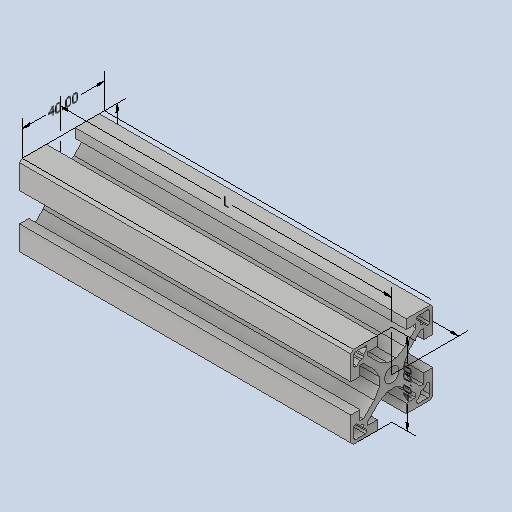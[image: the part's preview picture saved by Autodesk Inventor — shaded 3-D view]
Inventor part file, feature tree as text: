
AUTODESK INVENTOR PART (.ipt)
format: ipt  version: 2023 (Build 270158000, 158)  size: 289,792 bytes
history: native  units: mm
features: other x125, extrude x1, sketch x1
ambient origin geometry x8: Origin, YZ Plane, XZ Plane, XY Plane, X Axis, Y Axis, Z Axis, Center Point
bodies: Solid1 (feature_tree)
feature tree (127):
  other  "Annotations"
  extrude  "Extrusion1"  [1 undecoded]
  other  "CS_ANBAU_HINTEN_LINKS_XY"
  other  "CS_ANBAU_HINTEN_LINKS_YZ"
  other  "CS_ANBAU_HINTEN_LINKS_ZX"
  other  "CS_ANBAU_HINTEN_LINKS_X"
  other  "CS_ANBAU_HINTEN_LINKS_Y"
  other  "CS_ANBAU_HINTEN_LINKS_Z"
  other  "CS_ANBAU_HINTEN_LINKS_Center"
  other  "CS_ANBAU_HINTEN_OBEN_XY"
  other  "CS_ANBAU_HINTEN_OBEN_YZ"
  other  "CS_ANBAU_HINTEN_OBEN_ZX"
  other  "CS_ANBAU_HINTEN_OBEN_X"
  other  "CS_ANBAU_HINTEN_OBEN_Y"
  other  "CS_ANBAU_HINTEN_OBEN_Z"
  other  "CS_ANBAU_HINTEN_OBEN_Center"
  other  "CS_ANBAU_HINTEN_RECHTS_XY"
  other  "CS_ANBAU_HINTEN_RECHTS_YZ"
  other  "CS_ANBAU_HINTEN_RECHTS_ZX"
  other  "CS_ANBAU_HINTEN_RECHTS_X"
  other  "CS_ANBAU_HINTEN_RECHTS_Y"
  other  "CS_ANBAU_HINTEN_RECHTS_Z"
  other  "CS_ANBAU_HINTEN_RECHTS_Center"
  other  "CS_ANBAU_HINTEN_UNTEN_XY"
  other  "CS_ANBAU_HINTEN_UNTEN_YZ"
  other  "CS_ANBAU_HINTEN_UNTEN_ZX"
  other  "CS_ANBAU_HINTEN_UNTEN_X"
  other  "CS_ANBAU_HINTEN_UNTEN_Y"
  other  "CS_ANBAU_HINTEN_UNTEN_Z"
  other  "CS_ANBAU_HINTEN_UNTEN_Center"
  other  "CS_ANBAU_QUER_XY"
  other  "CS_ANBAU_QUER_YZ"
  other  "CS_ANBAU_QUER_ZX"
  other  "CS_ANBAU_QUER_X"
  other  "CS_ANBAU_QUER_Y"
  other  "CS_ANBAU_QUER_Z"
  other  "CS_ANBAU_QUER_Center"
  other  "CS_ANBAU_QUER_1_XY"
  other  "CS_ANBAU_QUER_1_YZ"
  other  "CS_ANBAU_QUER_1_ZX"
  other  "CS_ANBAU_QUER_1_X"
  other  "CS_ANBAU_QUER_1_Y"
  other  "CS_ANBAU_QUER_1_Z"
  other  "CS_ANBAU_QUER_1_Center"
  other  "CS_ANBAU_VORNE_LINKS_XY"
  other  "CS_ANBAU_VORNE_LINKS_YZ"
  other  "CS_ANBAU_VORNE_LINKS_ZX"
  other  "CS_ANBAU_VORNE_LINKS_X"
  other  "CS_ANBAU_VORNE_LINKS_Y"
  other  "CS_ANBAU_VORNE_LINKS_Z"
  other  "CS_ANBAU_VORNE_LINKS_Center"
  other  "CS_ANBAU_VORNE_OBEN_XY"
  other  "CS_ANBAU_VORNE_OBEN_YZ"
  other  "CS_ANBAU_VORNE_OBEN_ZX"
  other  "CS_ANBAU_VORNE_OBEN_X"
  other  "CS_ANBAU_VORNE_OBEN_Y"
  other  "CS_ANBAU_VORNE_OBEN_Z"
  other  "CS_ANBAU_VORNE_OBEN_Center"
  other  "CS_ANBAU_VORNE_RECHTS_XY"
  other  "CS_ANBAU_VORNE_RECHTS_YZ"
  other  "CS_ANBAU_VORNE_RECHTS_ZX"
  other  "CS_ANBAU_VORNE_RECHTS_X"
  other  "CS_ANBAU_VORNE_RECHTS_Y"
  other  "CS_ANBAU_VORNE_RECHTS_Z"
  other  "CS_ANBAU_VORNE_RECHTS_Center"
  other  "CS_ANBAU_VORNE_UNTEN_XY"
  other  "CS_ANBAU_VORNE_UNTEN_YZ"
  other  "CS_ANBAU_VORNE_UNTEN_ZX"
  other  "CS_ANBAU_VORNE_UNTEN_X"
  other  "CS_ANBAU_VORNE_UNTEN_Y"
  other  "CS_ANBAU_VORNE_UNTEN_Z"
  other  "CS_ANBAU_VORNE_UNTEN_Center"
  other  "p1_XY"
  other  "p1_YZ"
  other  "p1_ZX"
  other  "p1_X"
  other  "p1_Y"
  other  "p1_Z"
  other  "p1_Center"
  other  "p2_XY"
  other  "p2_YZ"
  other  "p2_ZX"
  other  "p2_X"
  other  "p2_Y"
  other  "p2_Z"
  other  "p2_Center"
  other  "p3_XY"
  other  "p3_YZ"
  other  "p3_ZX"
  other  "p3_X"
  other  "p3_Y"
  other  "p3_Z"
  other  "p3_Center"
  other  "p4_XY"
  other  "p4_YZ"
  other  "p4_ZX"
  other  "p4_X"
  other  "p4_Y"
  other  "p4_Z"
  other  "p4_Center"
  other  "p5_XY"
  other  "p5_YZ"
  other  "p5_ZX"
  other  "p5_X"
  other  "p5_Y"
  other  "p5_Z"
  other  "p5_Center"
  other  "pm1_XY"
  other  "pm1_YZ"
  other  "pm1_ZX"
  other  "pm1_X"
  other  "pm1_Y"
  other  "pm1_Z"
  other  "pm1_Center"
  other  "pm2_XY"
  other  "pm2_YZ"
  other  "pm2_ZX"
  other  "pm2_X"
  other  "pm2_Y"
  other  "pm2_Z"
  other  "pm2_Center"
  sketch  "Skizze_1"  dims[d0=161.0mm d1=0.0mm d2=0.0mm d3=0.0mm d4=0.0mm d5=0.0mm d6=0.0mm d10=161.0mm d11=161.0mm d7=40.0mm d8=40.0mm d9=40.0mm]
  other  "Linear Dimension 1"
  other  "Linear Dimension 2"
  other  "Linear Dimension 3"
  other  "Linear Dimension 4"
  other  "Linear Dimension 5"
note: 1 required parameter value undecoded (feature->parameter linkage not recoverable at this tier; creation-order binding heuristic only, values carry confidence <= 0.55)
